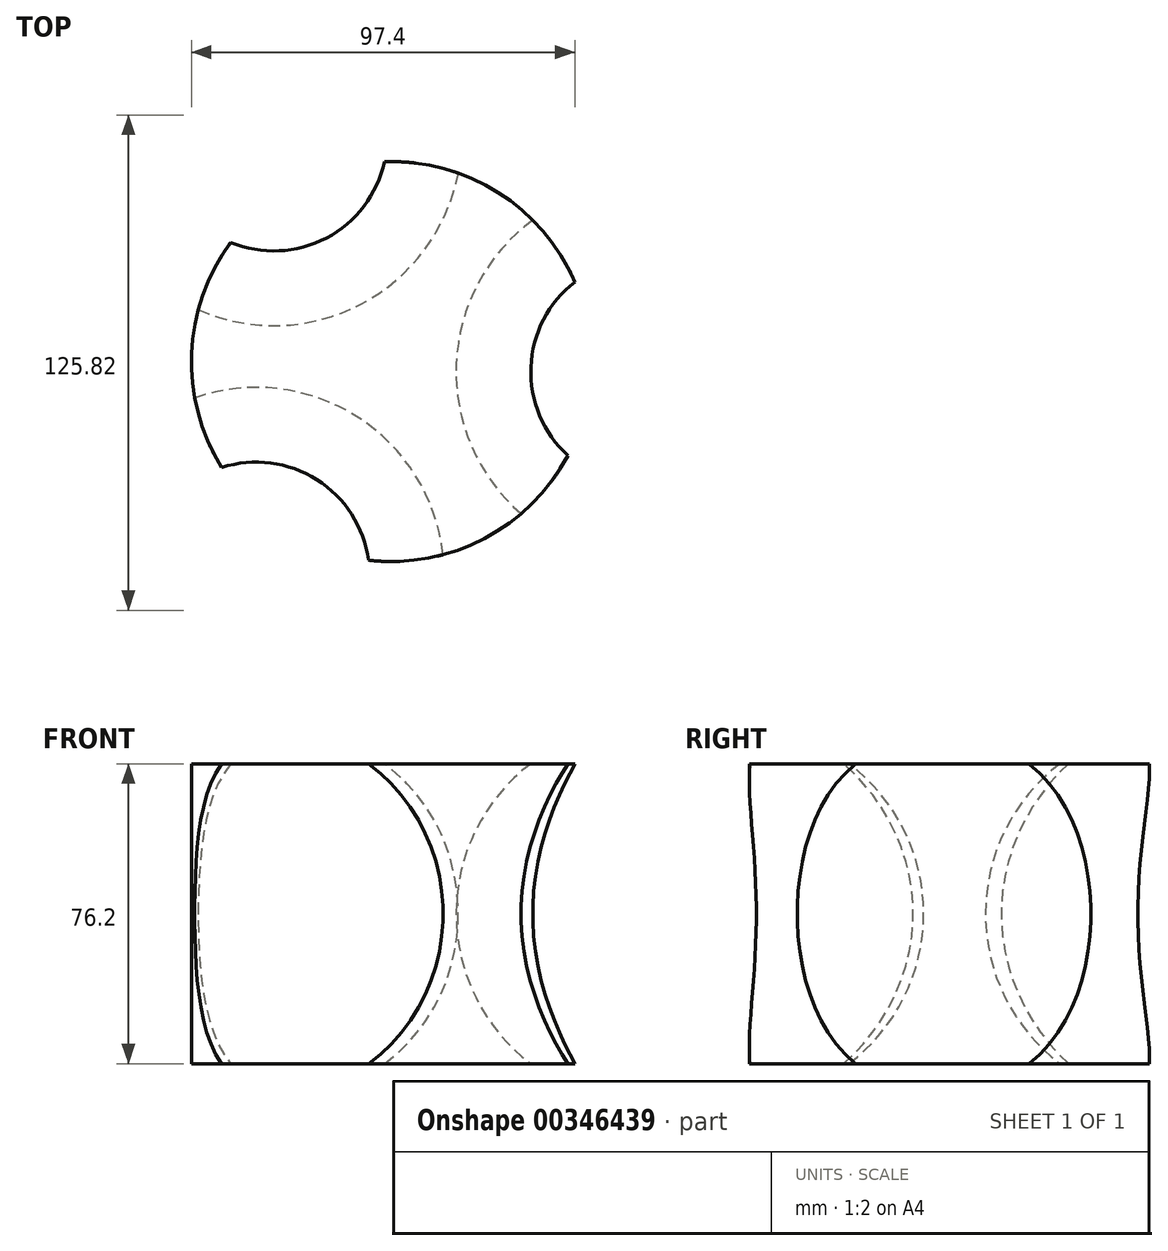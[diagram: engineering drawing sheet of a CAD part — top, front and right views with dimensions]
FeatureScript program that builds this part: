
annotation { "Feature Type Name" : "Feature", "Feature Type Description" : "" }
export const myFeature = defineFeature(function(context is Context, id is Id, definition is map)
    precondition{}
    {
        {
            var Q0;
            Q0=qCreatedBy(makeId("Top.planeOp"),FACE);
            var sketch = newSketch(context, id + "F0", { "sketchPlane" : qUnion([Q0])});
            skCircle(sketch, "E0", {"center": v(-96.8, 47.63) * mm, "radius": 50.8 * mm});
            skSolve(sketch);
        }
        {
            var Q0;
            Q0=makeQuery(id+"F0.imprint","IMPRINT",FACE,{"disambiguationData":[TD([[makeQuery(id+"F0.imprint","IMPRINT",EDGE,{"derivedFrom":sQuery(id+"F0.wireOp",EDGE,"E0")}),1.0]])]});
            var Q1;
            Q1=makeQuery(id+"F0.imprint","IMPRINT",FACE,{"disambiguationData":[TD([[makeQuery(id+"F0.imprint","IMPRINT",EDGE,{"derivedFrom":sQuery(id+"F0.wireOp",EDGE,"b6Zq218z-3GvH-4pmL-ln8l-ksN4OYJSZoCg")}),1.0]])]});
            var Q2;
            {var subQ1=sQuery(id+"F0.wireOp",EDGE,"zkDEctZs-1OYL-zxim-jiIC-K36yCcyzUPsu");var subQ4=sQuery(id+"F0.wireOp",EDGE,"7MTy1LFg-0odL-U7wn-hv3A-6P9JwYrrFmU3");var subQ5=makeQuery(id+"F0.imprint","INTERSECT",VERTEX,{"disambiguationData":[OD(0.0)],"derivedFrom":[subQ1,subQ4]});Q2=makeQuery(id+"F0.imprint","IMPRINT",FACE,{"disambiguationData":[TD([[makeQuery(id+"F0.imprint","IMPRINT",EDGE,{"disambiguationData":[TD([[subQ5,1.0]])],"derivedFrom":subQ1}),1.0]])]});}
            extrude(context, id + "F1", {"entities" : qUnion([Q0, Q1, Q2]), "depth" : 38.1 * mm, "hasSecondDirection" : true, "secondDirectionOppositeDirection" : true, "secondDirectionDepth" : 38.1 * mm});
        }
        {
            var Q0;
            Q0=qCreatedBy(makeId("Top.planeOp"),FACE);
            var sketch = newSketch(context, id + "F2", { "sketchPlane" : qUnion([Q0])});
            skCircle(sketch, "E1.0.0", {"center": v(-96.8, 47.63) * mm, "radius": 50.8 * mm});
            skCircle(sketch, "E2", {"center": v(-96.8, 47.63) * mm, "radius": 16.51 * mm});
            skCircle(sketch, "E3", {"center": v(-32.58, 45.07) * mm, "radius": 47.75 * mm});
            skLineSegment(sketch, "E4", {"start": v(-32.58, 45.07) * mm, "end": v(-32.58, 92.82) * mm});
            skLineSegment(sketch, "E5", {"start": v(-32.58, -2.69) * mm, "end": v(-32.58, 92.82) * mm});
            skCircle(sketch, "E6.1.0", {"center": v(-126.68, 104.51) * mm, "radius": 47.75 * mm});
            skLineSegment(sketch, "E7", {"start": v(-88.4, -28.07) * mm, "end": v(-131.12, -6.7) * mm});
            skLineSegment(sketch, "E8", {"start": v(-131.12, -6.7) * mm, "end": v(-173.82, 14.66) * mm});
            skArc(sketch, "E9", {"start": v(-173.82, 14.66) * mm, "mid": v(-152.48, -49.41) * mm, "end": v(-88.4, -28.07) * mm});
            skSolve(sketch);
        }
        {
            var Q0;
            {var subQ0=sQuery(id+"F2.wireOp",EDGE,"E5");var subQ4=makeQuery(id+"F2.imprint","IMPRINT",VERTEX,{"derivedFrom":subQ0});Q0=makeQuery(id+"F2.imprint","IMPRINT",FACE,{"disambiguationData":[TD([[makeQuery(id+"F2.imprint","IMPRINT",EDGE,{"disambiguationData":[TD([[subQ4,1.0]])],"derivedFrom":subQ0}),-1.0]])]});}
            var Q1;
            Q1=sQuery(id+"F2.wireOp",EDGE,"E3");
            var Q2;
            Q2=sQuery(id+"F2.wireOp",EDGE,"E4");
            revolve(context, id + "F3", {"operationType" : NewBodyOperationType.REMOVE, "entities" : qUnion([Q0]), "surfaceEntities" : qUnion([Q1]), "axis" : qUnion([Q2]), "revolveType" : RevolveType.FULL, "oppositeDirection" : true});
        }
        {
            var Q0;
            Q0=qCreatedBy(makeId("Top.planeOp"),FACE);
            var sketch = newSketch(context, id + "F4", { "sketchPlane" : qUnion([Q0])});
            skLineSegment(sketch, "E10.0", {"start": v(-131.12, -6.7) * mm, "end": v(-173.82, 14.66) * mm});
            skLineSegment(sketch, "E11.0", {"start": v(-88.4, -28.07) * mm, "end": v(-131.12, -6.7) * mm});
            skArc(sketch, "E12.0", {"start": v(-173.82, 14.66) * mm, "mid": v(-152.48, -49.41) * mm, "end": v(-88.4, -28.07) * mm});
            skSolve(sketch);
        }
        {
            var Q0;
            Q0=qSketchRegion(id+"F4",true);
            var Q1;
            Q1=sQuery(id+"F4.wireOp",EDGE,"E10.0");
            revolve(context, id + "F5", {"operationType" : NewBodyOperationType.REMOVE, "entities" : qUnion([Q0]), "axis" : qUnion([Q1]), "revolveType" : RevolveType.FULL, "oppositeDirection" : true});
        }
        {
            var Q0;
            Q0=qCreatedBy(makeId("Top.planeOp"),FACE);
            var sketch = newSketch(context, id + "F6", { "sketchPlane" : qUnion([Q0])});
            skLineSegment(sketch, "E13", {"start": v(-170.33, 85.13) * mm, "end": v(-126.68, 104.51) * mm});
            skLineSegment(sketch, "E14", {"start": v(-126.68, 104.51) * mm, "end": v(-83.04, 123.9) * mm});
            skArc(sketch, "E15", {"start": v(-83.04, 123.9) * mm, "mid": v(-146.07, 148.15) * mm, "end": v(-170.33, 85.13) * mm});
            skSolve(sketch);
        }
        {
            var Q0;
            Q0=qSketchRegion(id+"F6",true);
            var Q1;
            Q1=sQuery(id+"F6.wireOp",EDGE,"E13");
            revolve(context, id + "F7", {"operationType" : NewBodyOperationType.REMOVE, "entities" : qUnion([Q0]), "axis" : qUnion([Q1]), "revolveType" : RevolveType.FULL, "oppositeDirection" : true});
        }
    });
